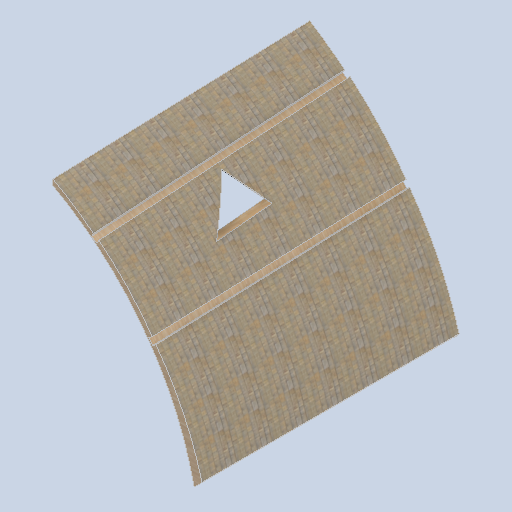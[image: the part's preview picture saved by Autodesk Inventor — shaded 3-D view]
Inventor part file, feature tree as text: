
AUTODESK INVENTOR PART (.ipt)
format: ipt  version: 2024.2 (Build 282272000, 272)  size: 377,344 bytes
history: native  units: in
note: dims shown in document units (in); Inventor stores cm internally (conversion verified against a paired STEP export)
features: other x3, sketch x2, plane x2
ambient origin geometry x8: Origin, YZ Plane, XZ Plane, XY Plane, X Axis, Y Axis, Z Axis, Center Point
bodies: Solid1 (feature_tree)
feature tree (7):
  other  "panel_block_03_MIR.ipt"
  other  "Solid1::panel_block_03_MIR.ipt"
  other  "TaggingFeature1"
  sketch  "Sketch1"  dims[d0=0.3937in]
  sketch  "Sketch2"
  plane  "Work Plane1"
  plane  "Work Plane2"
